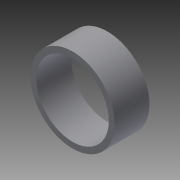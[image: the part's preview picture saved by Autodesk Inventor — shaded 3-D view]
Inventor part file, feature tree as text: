
AUTODESK INVENTOR PART (.ipt)
format: ipt  version: 2013 (Build 170138000, 138)  size: 80,896 bytes
history: native  units: in
note: dims shown in document units (in); Inventor stores cm internally (conversion verified against a paired STEP export)
features: extrude x1, sketch x1
ambient origin geometry x8: Origin, YZ Plane, XZ Plane, XY Plane, X Axis, Y Axis, Z Axis, Center Point
bodies: Solid1 (feature_tree)
feature tree (2):
  extrude  "Extrusion1"  Depth=1.25in
  sketch  "Sketch1"  dims[d0=1.45in d1=1.25in d2=0.6in d3=0.0in]
